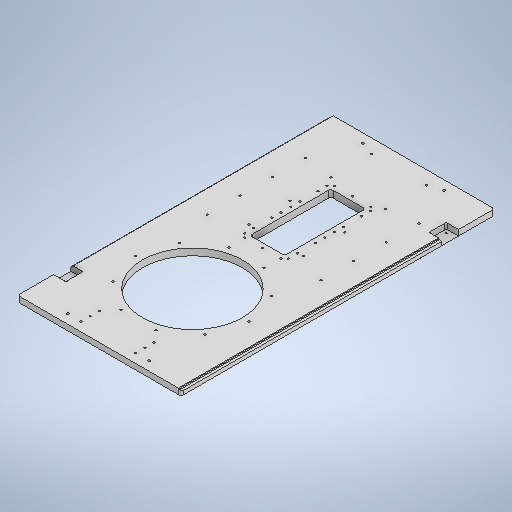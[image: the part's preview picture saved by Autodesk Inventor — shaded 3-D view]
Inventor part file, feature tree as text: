
AUTODESK INVENTOR PART (.ipt)
format: ipt  version: 2025 (Build 290162000, 162)  size: 578,048 bytes
history: native  units: in
note: dims shown in document units (in); Inventor stores cm internally (conversion verified against a paired STEP export)
features: sketch x17, extrude x6, hole x5, fillet x3, chamfer x3, plane x2
ambient origin geometry x8: Origin, YZ Plane, XZ Plane, XY Plane, X Axis, Y Axis, Z Axis, Center Point
bodies: Solid1 (feature_tree)
feature tree (36):
  extrude  "Base Cover"  Depth=14.1732in
  sketch  "Sketch2"  dims[d5=8.6614in d6=0.0in d7=0.0in]
  extrude  "Cylinder Hole"  Depth=0.5906in
  plane  "Work Plane1"
  hole  "Hole3"  [1 undecoded]
  sketch  "Sketch7"  dims[d69=0.1575in d70=3.937in d72=360.0deg]
  plane  "Work Plane2"
  hole  "Hole4"  [1 undecoded]
  sketch  "Sketch9"  dims[d82=1.063in]
  fillet  "Rounded Side Corners"  Radius=7.0625in
  chamfer  "Chamfer1"  Distance=3.937in Angle=360.0deg
  chamfer  "Chamfer2"  Distance=0.1969in
  extrude  "Magnet Seats"  Depth=0.3937in TaperAngle=45.0deg
  hole  "Hole5"  [1 undecoded]
  chamfer  "Chamfer5"  Distance=0.1181in
  hole  "Hole6"  [1 undecoded]
  sketch  "Sketch15"  dims[d85=1.4961in]
  extrude  "Extrusion11"  Depth=0.3937in TaperAngle=0.0deg
  fillet  "Fillet3"  Radius=0.748in
  hole  "Hole7"  [1 undecoded]
  fillet  "Rounded Bottom Corners"  Radius=0.8661in
  extrude  "Side Rail_L"  Depth=0.3937in
  extrude  "Side Rail_R"  Depth=0.3937in
  sketch  "Sketch1"  dims[d0=14.1732in d1=27.1654in]
  sketch  "Sketch6"  dims[d68=9.8425in]
  sketch  "Sketch8"  dims[d74=0.1628in d75=0.3937in d76=0.1575in d77=0.0787in d78=90.0deg d79=0.3937in d80=0.8108in]
  sketch  "Sketch Circular Pattern4"  dims[d57=0.1936in d58=0.1969in d59=0.1575in d60=0.0787in d61=90.0deg d62=0.1969in d63=0.8108in]
  sketch  "Sketch11"  dims[d83=1.063in]
  sketch  "Sketch12"  dims[d84=1.4961in]
  sketch  "Sketch Rectangular Pattern1"  dims[d2=0.5906in d3=0.0in d4=8.0709in]
  sketch  "Sketch Rectangular Pattern2"  dims[d8=10.6299in d50=5.9055in d55=7.0625in]
  sketch  "Sketch Rectangular Pattern3"  dims[d56=25.5906in]
  sketch  "Sketch Rectangular Pattern4"  dims[d64=10.3543in]
  sketch  "Sketch Rectangular Pattern5"  dims[d65=10.6299in]
  sketch  "Sketch16"  dims[d86=3.1102in]
  sketch  "Sketch17"  dims[d87=3.1102in d88=0.1969in d89=0.0984in d90=0.0787in d91=45.0deg d92=0.0984in d93=0.0787in d94=45.0deg d95=0.1181in d96=0.1181in d97=0.4951in d98=0.0in d109=0.748in d110=0.315in d111=0.8661in d112=0.748in d113=0.1299in d114=0.1299in d115=0.1299in d116=0.1299in d118=0.315in d119=0.8661in d120=0.748in d121=0.748in d122=0.1276in d123=0.315in d124=0.1575in d125=0.0787in d126=90.0deg d127=0.315in d128=0.8108in d129=0.0138in d130=0.0787in d131=45.0deg d146=3.9469in d147=0.7874in d148=0.3937in d149=0.1575in d150=3.937in d152=1.1811in d153=0.3937in d155=0.3937in d157=0.1575in d158=1.1811in d160=0.7874in d161=0.3937in d163=0.3937in d165=9.8425in d166=0.1575in d167=2.9528in d168=1.1811in d169=3.1496in d171=1.4173in d172=0.3937in d174=0.3937in d176=0.1628in d177=0.3937in d178=0.1575in d179=0.0787in d180=90.0deg d181=0.3937in d182=0.8108in d191=3.0in d192=7.0in d193=6.4961in d194=0.8312in d195=0.0in d196=0.1969in d197=0.3937in d198=0.1969in d199=1.9685in d201=0.7874in d202=0.3937in d204=0.3937in d206=0.3189in d207=0.1969in d208=0.3189in d209=1.9685in d211=0.7874in d212=0.3937in d214=0.3937in d216=0.1628in d217=0.3937in d218=0.1575in d219=0.0787in d220=90.0deg d221=0.3937in d222=0.8108in d230=0.2756in d231=0.2362in d232=0.0787in d233=0.1378in d234=0.503in d235=0.5906in d236=0.0in d237=0.1378in d238=0.0787in d239=0.2362in d240=0.503in d241=0.3937in d242=0.0in d26=0.0394in d27=0.0394in d28=0.0394in d29=0.0059in d30=0.0098in d31=0.0148in d32=0.5635in d33=0.0295in d34=0.8108in d35=0.0025in d36=0.0295in d37=0.0148in d66=0.0197in d67=0.0344in]
note: 5 required parameter values undecoded (feature->parameter linkage not recoverable at this tier; creation-order binding heuristic only, values carry confidence <= 0.55)
